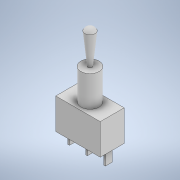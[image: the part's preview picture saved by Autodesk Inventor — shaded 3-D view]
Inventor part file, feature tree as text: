
AUTODESK INVENTOR PART (.ipt)
format: ipt  version: 2021 (Build 250183000, 183)  size: 171,008 bytes
history: native  units: mm
features: sketch x5, extrude x4, revolve x1
ambient origin geometry x8: Origin, YZ Plane, XZ Plane, XY Plane, X Axis, Y Axis, Z Axis, Center Point
bodies: Solid1 (feature_tree)
feature tree (10):
  extrude  "Extrusion1"  Depth=9.0mm
  extrude  "Extrusion2"  Depth=4.5mm
  extrude  "Extrusion3"  Depth=0.5mm
  extrude  "Extrusion4"  Depth=0.5mm
  revolve  "Revolution1"  [1 undecoded]
  sketch  "Sketch1"  dims[d0=13.0mm d1=9.0mm]
  sketch  "Sketch2"  dims[d2=4.5mm d3=6.5mm]
  sketch  "Sketch3"  dims[d4=7.0mm d5=0.0mm d6=0.5mm]
  sketch  "Sketch4"  dims[d7=0.5mm d8=0.5mm]
  sketch  "Sketch5"  dims[d9=1.0mm d10=1.0mm d11=6.25mm d12=6.25mm d13=2.0mm d14=2.0mm d15=2.0mm d16=2.5mm d17=4.0mm d18=0.0mm d19=5.3mm d20=9.0mm d21=0.0mm d22=0.0mm d23=0.1mm d24=0.5mm d25=0.5mm d26=3.0mm d27=0.0mm d28=10.0mm d29=1.5mm d30=1.1mm d31=1.0mm d32=1.6mm d33=90.0deg]
note: 1 required parameter value undecoded (feature->parameter linkage not recoverable at this tier; creation-order binding heuristic only, values carry confidence <= 0.55)
